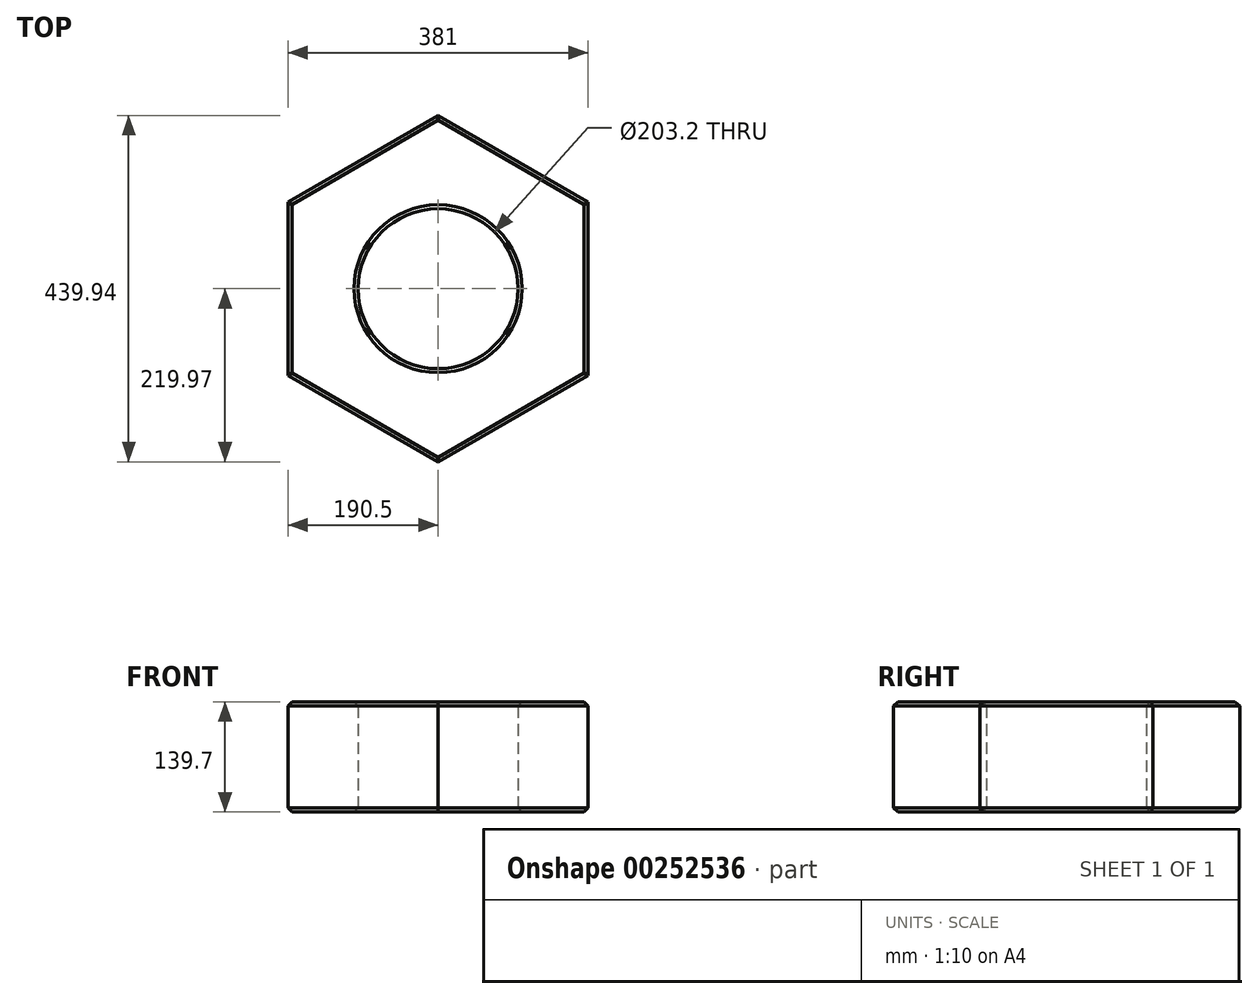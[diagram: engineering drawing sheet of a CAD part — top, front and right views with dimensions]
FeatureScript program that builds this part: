
annotation { "Feature Type Name" : "Feature", "Feature Type Description" : "" }
export const myFeature = defineFeature(function(context is Context, id is Id, definition is map)
    precondition{}
    {
        {
            var Q0;
            Q0=qCreatedBy(makeId("Top.planeOp"),FACE);
            var sketch = newSketch(context, id + "F0", { "sketchPlane" : qUnion([Q0])});
            skCircle(sketch, "E0", {"center": v(0, 0) * mm, "radius": 101.6 * mm});
            skCircle(sketch, "E1.cCircle", {"center": v(0, 0) * mm, "radius": 190.5 * mm, "construction": true});
            skLineSegment(sketch, "E1.0", {"start": v(-190.5, -109.99) * mm, "end": v(-190.5, 109.99) * mm});
            skLineSegment(sketch, "E1.1", {"start": v(-190.5, 109.99) * mm, "end": v(0, 219.97) * mm});
            skLineSegment(sketch, "E1.2", {"start": v(0, 219.97) * mm, "end": v(190.5, 109.99) * mm});
            skLineSegment(sketch, "E1.3", {"start": v(190.5, 109.99) * mm, "end": v(190.5, -109.99) * mm});
            skLineSegment(sketch, "E1.4", {"start": v(190.5, -109.99) * mm, "end": v(0, -219.97) * mm});
            skLineSegment(sketch, "E1.5", {"start": v(0, -219.97) * mm, "end": v(-190.5, -109.99) * mm});
            skPoint(sketch, "E1.0.midPoint", {"position": v(-190.5, 0) * mm});
            skSolve(sketch);
        }
        {
            var Q0;
            Q0=makeQuery(id+"F0.imprint","IMPRINT",FACE,{"disambiguationData":[TD([[makeQuery(id+"F0.imprint","IMPRINT",EDGE,{"derivedFrom":sQuery(id+"F0.wireOp",EDGE,"E0")}),-1.0]])]});
            extrude(context, id + "F1", {"entities" : qUnion([Q0]), "depth" : 139.7 * mm});
        }
        {
            var Q0;
            Q0=makeQuery(id+"F1.opExtrude","CAP_FACE",FACE,{"disambiguationData":[OSD([sQuery(id+"F0.wireOp",EDGE,"E0"),sQuery(id+"F0.wireOp",EDGE,"E1.0"),sQuery(id+"F0.wireOp",EDGE,"E1.1"),sQuery(id+"F0.wireOp",EDGE,"E1.2"),sQuery(id+"F0.wireOp",EDGE,"E1.3"),sQuery(id+"F0.wireOp",EDGE,"E1.4"),sQuery(id+"F0.wireOp",EDGE,"E1.5")])],"isStart":false});
            var Q1;
            Q1=makeQuery(id+"F1.opExtrude","CAP_FACE",FACE,{"disambiguationData":[OSD([sQuery(id+"F0.wireOp",EDGE,"E0"),sQuery(id+"F0.wireOp",EDGE,"E1.0"),sQuery(id+"F0.wireOp",EDGE,"E1.1"),sQuery(id+"F0.wireOp",EDGE,"E1.2"),sQuery(id+"F0.wireOp",EDGE,"E1.3"),sQuery(id+"F0.wireOp",EDGE,"E1.4"),sQuery(id+"F0.wireOp",EDGE,"E1.5")])],"isStart":true});
            chamfer(context, id + "F2", {"entities" : qUnion([Q0, Q1]), "width" : 5.08 * mm, "tangentPropagation" : true});
        }
    });
